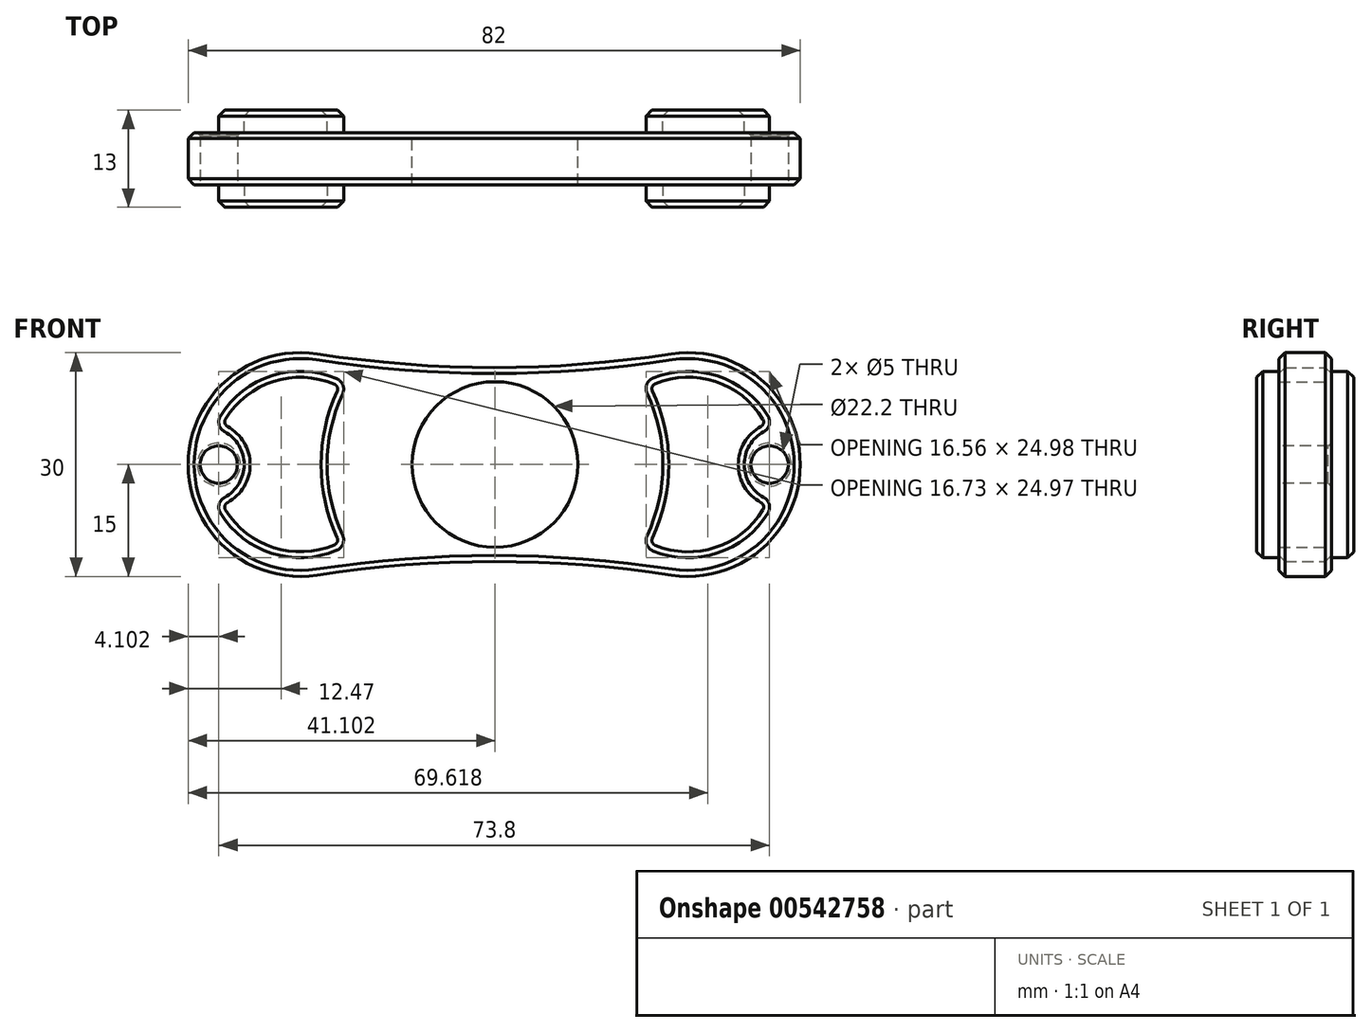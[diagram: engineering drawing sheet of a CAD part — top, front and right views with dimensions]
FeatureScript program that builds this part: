
annotation { "Feature Type Name" : "Feature", "Feature Type Description" : "" }
export const myFeature = defineFeature(function(context is Context, id is Id, definition is map)
    precondition{}
    {
        {
            var Q0;
            Q0=qCreatedBy(makeId("Front.planeOp"),FACE);
            var sketch = newSketch(context, id + "F0", { "sketchPlane" : qUnion([Q0])});
            skCircle(sketch, "E0", {"center": v(-1.84, 0) * mm, "radius": 11.1 * mm});
            skArc(sketch, "E1", {"start": v(-25.64, 14.82) * mm, "mid": v(-42.94, 0) * mm, "end": v(-25.64, -14.82) * mm});
            skArc(sketch, "E2", {"start": v(-25.64, 14.82) * mm, "mid": v(-1.94, 13) * mm, "end": v(21.77, 14.82) * mm});
            skArc(sketch, "E3", {"start": v(21.77, -14.82) * mm, "mid": v(-1.94, -13) * mm, "end": v(-25.64, -14.82) * mm});
            skArc(sketch, "E4.trimOffspring", {"start": v(21.77, -14.82) * mm, "mid": v(39.06, 0) * mm, "end": v(21.77, 14.82) * mm});
            skSolve(sketch);
        }
        {
            var Q0;
            Q0=makeQuery(id+"F0.imprint","IMPRINT",FACE,{"disambiguationData":[TD([[makeQuery(id+"F0.imprint","IMPRINT",EDGE,{"derivedFrom":sQuery(id+"F0.wireOp",EDGE,"E0")}),-1.0]])]});
            extrude(context, id + "F1", {"entities" : qUnion([Q0]), "depth" : 7 * mm, "offsetDistance" : 25 * mm});
        }
        {
            var Q0;
            Q0=makeQuery(id+"F1.opExtrude","CAP_EDGE",EDGE,{"disambiguationData":[OSD([sQuery(id+"F0.wireOp",EDGE,"E1")])],"isStart":false});
            var Q1;
            Q1=makeQuery(id+"F1.opExtrude","CAP_EDGE",EDGE,{"disambiguationData":[OSD([sQuery(id+"F0.wireOp",EDGE,"E3")])],"isStart":false});
            var Q2;
            Q2=makeQuery(id+"F1.opExtrude","CAP_EDGE",EDGE,{"disambiguationData":[OSD([sQuery(id+"F0.wireOp",EDGE,"E3")])],"isStart":true});
            chamfer(context, id + "F2", {"entities" : qUnion([Q0, Q1, Q2]), "width" : .8 * mm, "tangentPropagation" : true});
        }
        {
            var Q0;
            Q0=makeQuery(id+"F1.opExtrude","CAP_FACE",FACE,{"disambiguationData":[OSD([sQuery(id+"F0.wireOp",EDGE,"E0"),sQuery(id+"F0.wireOp",EDGE,"E1"),sQuery(id+"F0.wireOp",EDGE,"E2"),sQuery(id+"F0.wireOp",EDGE,"E3"),sQuery(id+"F0.wireOp",EDGE,"E4.trimOffspring")])],"isStart":false});
            var sketch = newSketch(context, id + "F3", { "sketchPlane" : qUnion([Q0])});
            skCircle(sketch, "E5", {"center": v(-27.94, 0) * mm, "radius": 12.5 * mm});
            skCircle(sketch, "E6", {"center": v(24.06, 0) * mm, "radius": 12.5 * mm});
            skSolve(sketch);
        }
        {
            var Q0;
            Q0 = qSketchRegion(id + "F3", true);
            extrude(context, id + "F4", {"entities" : qUnion([Q0]), "operationType" : NewBodyOperationType.ADD, "depth" : 3 * mm, "offsetDistance" : 25 * mm});
        }
        {
            var Q0;
            Q0=makeQuery(id+"F1.opExtrude","CAP_FACE",FACE,{"disambiguationData":[OSD([sQuery(id+"F0.wireOp",EDGE,"E0"),sQuery(id+"F0.wireOp",EDGE,"E1"),sQuery(id+"F0.wireOp",EDGE,"E2"),sQuery(id+"F0.wireOp",EDGE,"E3"),sQuery(id+"F0.wireOp",EDGE,"E4.trimOffspring")])],"isStart":true});
            var sketch = newSketch(context, id + "F5", { "sketchPlane" : qUnion([Q0])});
            skCircle(sketch, "E7", {"center": v(-24.06, 0) * mm, "radius": 12.5 * mm});
            skCircle(sketch, "E8", {"center": v(27.94, 0) * mm, "radius": 12.5 * mm});
            skSolve(sketch);
        }
        {
            var Q0;
            Q0 = qSketchRegion(id + "F5", true);
            extrude(context, id + "F6", {"entities" : qUnion([Q0]), "operationType" : NewBodyOperationType.ADD, "depth" : 3 * mm, "offsetDistance" : 25 * mm});
        }
        {
            var Q0;
            Q0=makeQuery(id+"F4.opExtrude","CAP_FACE",FACE,{"disambiguationData":[OSD([sQuery(id+"F3.wireOp",EDGE,"E6")])],"isStart":false});
            var sketch = newSketch(context, id + "F7", { "sketchPlane" : qUnion([Q0])});
            skSolve(sketch);
        }
        {
            var Q0;
            Q0=makeQuery(id+"F4.opExtrude","CAP_FACE",FACE,{"disambiguationData":[OSD([sQuery(id+"F3.wireOp",EDGE,"E5")])],"isStart":false});
            var sketch = newSketch(context, id + "F8", { "sketchPlane" : qUnion([Q0])});
            skCircle(sketch, "E9", {"center": v(-1.84, 0) * mm, "radius": 22.5 * mm});
            skSolve(sketch);
        }
        {
            var Q0;
            Q0 = qSketchRegion(id + "F8", true);
            extrude(context, id + "F9", {"entities" : qUnion([Q0]), "operationType" : NewBodyOperationType.REMOVE, "oppositeDirection" : true, "depth" : 3 * mm, "offsetDistance" : 25 * mm});
        }
        {
            var Q0;
            Q0=makeQuery(id+"F6.opExtrude","CAP_FACE",FACE,{"disambiguationData":[OSD([sQuery(id+"F5.wireOp",EDGE,"E7")])],"isStart":false});
            var sketch = newSketch(context, id + "F10", { "sketchPlane" : qUnion([Q0])});
            skCircle(sketch, "E10", {"center": v(1.84, 0) * mm, "radius": 22.5 * mm});
            skSolve(sketch);
        }
        {
            var Q0;
            Q0 = qSketchRegion(id + "F10", true);
            extrude(context, id + "F11", {"entities" : qUnion([Q0]), "operationType" : NewBodyOperationType.REMOVE, "oppositeDirection" : true, "depth" : 3 * mm, "offsetDistance" : 25 * mm});
        }
        {
            var Q0;
            Q0=makeQuery(id+"F6.opExtrude","CAP_FACE",FACE,{"disambiguationData":[OSD([sQuery(id+"F5.wireOp",EDGE,"E7")])],"isStart":false});
            var sketch = newSketch(context, id + "F12", { "sketchPlane" : qUnion([Q0])});
            skCircle(sketch, "E11", {"center": v(-36.56, 0) * mm, "radius": 5 * mm});
            skSolve(sketch);
        }
        {
            var Q0;
            Q0 = qSketchRegion(id + "F12", true);
            extrude(context, id + "F13", {"entities" : qUnion([Q0]), "operationType" : NewBodyOperationType.REMOVE, "oppositeDirection" : true, "depth" : 3 * mm, "offsetDistance" : 25 * mm});
        }
        {
            var Q0;
            Q0=makeQuery(id+"F6.opExtrude","CAP_FACE",FACE,{"disambiguationData":[OSD([sQuery(id+"F5.wireOp",EDGE,"E8")])],"isStart":false});
            var sketch = newSketch(context, id + "F14", { "sketchPlane" : qUnion([Q0])});
            skCircle(sketch, "E12", {"center": v(40.44, 0) * mm, "radius": 5 * mm});
            skSolve(sketch);
        }
        {
            var Q0;
            Q0 = qSketchRegion(id + "F14", true);
            extrude(context, id + "F15", {"entities" : qUnion([Q0]), "operationType" : NewBodyOperationType.REMOVE, "oppositeDirection" : true, "depth" : 3 * mm, "offsetDistance" : 25 * mm});
        }
        {
            var Q0;
            Q0=makeQuery(id+"F4.opExtrude","CAP_FACE",FACE,{"disambiguationData":[OSD([sQuery(id+"F3.wireOp",EDGE,"E5")])],"isStart":false});
            var sketch = newSketch(context, id + "F16", { "sketchPlane" : qUnion([Q0])});
            skCircle(sketch, "E13", {"center": v(-40.44, 0) * mm, "radius": 5 * mm});
            skSolve(sketch);
        }
        {
            var Q0;
            Q0 = qSketchRegion(id + "F16", true);
            extrude(context, id + "F17", {"entities" : qUnion([Q0]), "operationType" : NewBodyOperationType.REMOVE, "oppositeDirection" : true, "depth" : 3 * mm, "offsetDistance" : 25 * mm});
        }
        {
            var Q0;
            Q0=makeQuery(id+"F7.imprint","IMPRINT",FACE,{"disambiguationData":[TD([[makeQuery(id+"F7.imprint","IMPRINT",EDGE,{"derivedFrom":makeQuery(id+"F4.opExtrude","CAP_EDGE",EDGE,{"disambiguationData":[OSD([sQuery(id+"F3.wireOp",EDGE,"E6")])],"isStart":false})}),1.0]])]});
            var sketch = newSketch(context, id + "F18", { "sketchPlane" : qUnion([Q0])});
            skCircle(sketch, "E14", {"center": v(36.56, 0) * mm, "radius": 5 * mm});
            skSolve(sketch);
        }
        {
            var Q0;
            Q0 = qSketchRegion(id + "F18", true);
            extrude(context, id + "F19", {"entities" : qUnion([Q0]), "operationType" : NewBodyOperationType.REMOVE, "oppositeDirection" : true, "depth" : 3 * mm, "offsetDistance" : 25 * mm});
        }
        {
            var Q0;
            Q0=makeQuery(id+"F17.boolean.opBoolean","INTERSECT",EDGE,{"disambiguationData":[OD(0.0)],"derivedFrom":[makeQuery(id+"F4.opExtrude","SWEPT_FACE",FACE,{"disambiguationData":[OSD([sQuery(id+"F3.wireOp",EDGE,"E5")])]}),makeQuery(id+"F17.opExtrude","SWEPT_FACE",FACE,{"disambiguationData":[OSD([sQuery(id+"F16.wireOp",EDGE,"E13")])]})]});
            var Q1;
            Q1=makeQuery(id+"F17.boolean.opBoolean","INTERSECT",EDGE,{"disambiguationData":[OD(1.0)],"derivedFrom":[makeQuery(id+"F4.opExtrude","SWEPT_FACE",FACE,{"disambiguationData":[OSD([sQuery(id+"F3.wireOp",EDGE,"E5")])]}),makeQuery(id+"F17.opExtrude","SWEPT_FACE",FACE,{"disambiguationData":[OSD([sQuery(id+"F16.wireOp",EDGE,"E13")])]})]});
            var Q2;
            Q2=makeQuery(id+"F9.boolean.opBoolean","INTERSECT",EDGE,{"disambiguationData":[OD(1.0)],"derivedFrom":[makeQuery(id+"F4.opExtrude","SWEPT_FACE",FACE,{"disambiguationData":[OSD([sQuery(id+"F3.wireOp",EDGE,"E5")])]}),makeQuery(id+"F9.opExtrude","SWEPT_FACE",FACE,{"disambiguationData":[OSD([sQuery(id+"F8.wireOp",EDGE,"E9")])]})]});
            var Q3;
            Q3=makeQuery(id+"F9.boolean.opBoolean","INTERSECT",EDGE,{"disambiguationData":[OD(0.0)],"derivedFrom":[makeQuery(id+"F4.opExtrude","SWEPT_FACE",FACE,{"disambiguationData":[OSD([sQuery(id+"F3.wireOp",EDGE,"E5")])]}),makeQuery(id+"F9.opExtrude","SWEPT_FACE",FACE,{"disambiguationData":[OSD([sQuery(id+"F8.wireOp",EDGE,"E9")])]})]});
            var Q4;
            Q4=makeQuery(id+"F9.boolean.opBoolean","INTERSECT",EDGE,{"disambiguationData":[OD(1.0)],"derivedFrom":[makeQuery(id+"F4.opExtrude","SWEPT_FACE",FACE,{"disambiguationData":[OSD([sQuery(id+"F3.wireOp",EDGE,"E6")])]}),makeQuery(id+"F9.opExtrude","SWEPT_FACE",FACE,{"disambiguationData":[OSD([sQuery(id+"F8.wireOp",EDGE,"E9")])]})]});
            var Q5;
            Q5=makeQuery(id+"F9.boolean.opBoolean","INTERSECT",EDGE,{"disambiguationData":[OD(0.0)],"derivedFrom":[makeQuery(id+"F4.opExtrude","SWEPT_FACE",FACE,{"disambiguationData":[OSD([sQuery(id+"F3.wireOp",EDGE,"E6")])]}),makeQuery(id+"F9.opExtrude","SWEPT_FACE",FACE,{"disambiguationData":[OSD([sQuery(id+"F8.wireOp",EDGE,"E9")])]})]});
            var Q6;
            Q6=makeQuery(id+"F19.boolean.opBoolean","INTERSECT",EDGE,{"disambiguationData":[OD(1.0)],"derivedFrom":[makeQuery(id+"F4.opExtrude","SWEPT_FACE",FACE,{"disambiguationData":[OSD([sQuery(id+"F3.wireOp",EDGE,"E6")])]}),makeQuery(id+"F19.opExtrude","SWEPT_FACE",FACE,{"disambiguationData":[OSD([sQuery(id+"F18.wireOp",EDGE,"E14")])]})]});
            var Q7;
            Q7=makeQuery(id+"F19.boolean.opBoolean","INTERSECT",EDGE,{"disambiguationData":[OD(0.0)],"derivedFrom":[makeQuery(id+"F4.opExtrude","SWEPT_FACE",FACE,{"disambiguationData":[OSD([sQuery(id+"F3.wireOp",EDGE,"E6")])]}),makeQuery(id+"F19.opExtrude","SWEPT_FACE",FACE,{"disambiguationData":[OSD([sQuery(id+"F18.wireOp",EDGE,"E14")])]})]});
            var Q8;
            Q8=makeQuery(id+"F11.boolean.opBoolean","INTERSECT",EDGE,{"disambiguationData":[OD(0.0)],"derivedFrom":[makeQuery(id+"F6.opExtrude","SWEPT_FACE",FACE,{"disambiguationData":[OSD([sQuery(id+"F5.wireOp",EDGE,"E8")])]}),makeQuery(id+"F11.opExtrude","SWEPT_FACE",FACE,{"disambiguationData":[OSD([sQuery(id+"F10.wireOp",EDGE,"E10")])]})]});
            var Q9;
            Q9=makeQuery(id+"F11.boolean.opBoolean","INTERSECT",EDGE,{"disambiguationData":[OD(1.0)],"derivedFrom":[makeQuery(id+"F6.opExtrude","SWEPT_FACE",FACE,{"disambiguationData":[OSD([sQuery(id+"F5.wireOp",EDGE,"E8")])]}),makeQuery(id+"F11.opExtrude","SWEPT_FACE",FACE,{"disambiguationData":[OSD([sQuery(id+"F10.wireOp",EDGE,"E10")])]})]});
            var Q10;
            Q10=makeQuery(id+"F15.boolean.opBoolean","INTERSECT",EDGE,{"disambiguationData":[OD(0.0)],"derivedFrom":[makeQuery(id+"F6.opExtrude","SWEPT_FACE",FACE,{"disambiguationData":[OSD([sQuery(id+"F5.wireOp",EDGE,"E8")])]}),makeQuery(id+"F15.opExtrude","SWEPT_FACE",FACE,{"disambiguationData":[OSD([sQuery(id+"F14.wireOp",EDGE,"E12")])]})]});
            var Q11;
            Q11=makeQuery(id+"F15.boolean.opBoolean","INTERSECT",EDGE,{"disambiguationData":[OD(1.0)],"derivedFrom":[makeQuery(id+"F6.opExtrude","SWEPT_FACE",FACE,{"disambiguationData":[OSD([sQuery(id+"F5.wireOp",EDGE,"E8")])]}),makeQuery(id+"F15.opExtrude","SWEPT_FACE",FACE,{"disambiguationData":[OSD([sQuery(id+"F14.wireOp",EDGE,"E12")])]})]});
            var Q12;
            Q12=makeQuery(id+"F11.boolean.opBoolean","INTERSECT",EDGE,{"disambiguationData":[OD(0.0)],"derivedFrom":[makeQuery(id+"F6.opExtrude","SWEPT_FACE",FACE,{"disambiguationData":[OSD([sQuery(id+"F5.wireOp",EDGE,"E7")])]}),makeQuery(id+"F11.opExtrude","SWEPT_FACE",FACE,{"disambiguationData":[OSD([sQuery(id+"F10.wireOp",EDGE,"E10")])]})]});
            var Q13;
            Q13=makeQuery(id+"F11.boolean.opBoolean","INTERSECT",EDGE,{"disambiguationData":[OD(1.0)],"derivedFrom":[makeQuery(id+"F6.opExtrude","SWEPT_FACE",FACE,{"disambiguationData":[OSD([sQuery(id+"F5.wireOp",EDGE,"E7")])]}),makeQuery(id+"F11.opExtrude","SWEPT_FACE",FACE,{"disambiguationData":[OSD([sQuery(id+"F10.wireOp",EDGE,"E10")])]})]});
            var Q14;
            Q14=makeQuery(id+"F13.boolean.opBoolean","INTERSECT",EDGE,{"disambiguationData":[OD(0.0)],"derivedFrom":[makeQuery(id+"F6.opExtrude","SWEPT_FACE",FACE,{"disambiguationData":[OSD([sQuery(id+"F5.wireOp",EDGE,"E7")])]}),makeQuery(id+"F13.opExtrude","SWEPT_FACE",FACE,{"disambiguationData":[OSD([sQuery(id+"F12.wireOp",EDGE,"E11")])]})]});
            var Q15;
            Q15=makeQuery(id+"F13.boolean.opBoolean","INTERSECT",EDGE,{"disambiguationData":[OD(1.0)],"derivedFrom":[makeQuery(id+"F6.opExtrude","SWEPT_FACE",FACE,{"disambiguationData":[OSD([sQuery(id+"F5.wireOp",EDGE,"E7")])]}),makeQuery(id+"F13.opExtrude","SWEPT_FACE",FACE,{"disambiguationData":[OSD([sQuery(id+"F12.wireOp",EDGE,"E11")])]})]});
            fillet(context, id + "F20", {"entities" : qUnion([Q0, Q1, Q2, Q3, Q4, Q5, Q6, Q7, Q8, Q9, Q10, Q11, Q12, Q13, Q14, Q15]), "radius" : 1.5 * mm, "tangentPropagation" : true, "allowEdgeOverflow" : false});
        }
        {
            var Q0;
            Q0=makeQuery(id+"F19.boolean.opBoolean","MERGE",FACE,{"derivedFrom":[makeQuery(id+"F17.boolean.opBoolean","MERGE",FACE,{"derivedFrom":[makeQuery(id+"F9.boolean.opBoolean","MERGE",FACE,{"derivedFrom":[makeQuery(id+"F1.opExtrude","CAP_FACE",FACE,{"disambiguationData":[OSD([sQuery(id+"F0.wireOp",EDGE,"E0"),sQuery(id+"F0.wireOp",EDGE,"E1"),sQuery(id+"F0.wireOp",EDGE,"E2"),sQuery(id+"F0.wireOp",EDGE,"E3"),sQuery(id+"F0.wireOp",EDGE,"E4.trimOffspring")])],"isStart":false}),makeQuery(id+"F9.opExtrude","CAP_FACE",FACE,{"disambiguationData":[OSD([sQuery(id+"F8.wireOp",EDGE,"E9")])],"isStart":false})]}),makeQuery(id+"F17.opExtrude","CAP_FACE",FACE,{"disambiguationData":[OSD([sQuery(id+"F16.wireOp",EDGE,"E13")])],"isStart":false})]}),makeQuery(id+"F19.opExtrude","CAP_FACE",FACE,{"disambiguationData":[OSD([sQuery(id+"F18.wireOp",EDGE,"E14")])],"isStart":false})]});
            var sketch = newSketch(context, id + "F21", { "sketchPlane" : qUnion([Q0])});
            skCircle(sketch, "E15", {"center": v(-38.84, 0) * mm, "radius": 2.5 * mm});
            skSolve(sketch);
        }
        {
            var Q0;
            Q0 = qSketchRegion(id + "F21", true);
            extrude(context, id + "F22", {"entities" : qUnion([Q0]), "operationType" : NewBodyOperationType.REMOVE, "oppositeDirection" : true, "depth" : 25 * mm, "offsetDistance" : 25 * mm});
        }
        {
            var Q0;
            Q0=makeQuery(id+"F19.boolean.opBoolean","MERGE",FACE,{"derivedFrom":[makeQuery(id+"F17.boolean.opBoolean","MERGE",FACE,{"derivedFrom":[makeQuery(id+"F9.boolean.opBoolean","MERGE",FACE,{"derivedFrom":[makeQuery(id+"F1.opExtrude","CAP_FACE",FACE,{"disambiguationData":[OSD([sQuery(id+"F0.wireOp",EDGE,"E0"),sQuery(id+"F0.wireOp",EDGE,"E1"),sQuery(id+"F0.wireOp",EDGE,"E2"),sQuery(id+"F0.wireOp",EDGE,"E3"),sQuery(id+"F0.wireOp",EDGE,"E4.trimOffspring")])],"isStart":false}),makeQuery(id+"F9.opExtrude","CAP_FACE",FACE,{"disambiguationData":[OSD([sQuery(id+"F8.wireOp",EDGE,"E9")])],"isStart":false})]}),makeQuery(id+"F17.opExtrude","CAP_FACE",FACE,{"disambiguationData":[OSD([sQuery(id+"F16.wireOp",EDGE,"E13")])],"isStart":false})]}),makeQuery(id+"F19.opExtrude","CAP_FACE",FACE,{"disambiguationData":[OSD([sQuery(id+"F18.wireOp",EDGE,"E14")])],"isStart":false})]});
            var sketch = newSketch(context, id + "F23", { "sketchPlane" : qUnion([Q0])});
            skCircle(sketch, "E16", {"center": v(34.96, 0) * mm, "radius": 2.5 * mm});
            skSolve(sketch);
        }
        {
            var Q0;
            Q0 = qSketchRegion(id + "F23", true);
            extrude(context, id + "F24", {"entities" : qUnion([Q0]), "operationType" : NewBodyOperationType.REMOVE, "oppositeDirection" : true, "depth" : 25 * mm, "offsetDistance" : 25 * mm});
        }
        {
            var Q0;
            Q0=makeQuery(id+"F22.boolean.opBoolean","COPY",EDGE,{"derivedFrom":makeQuery(id+"F22.opExtrude","CAP_EDGE",EDGE,{"disambiguationData":[OSD([sQuery(id+"F21.wireOp",EDGE,"E15")])],"isStart":true})});
            var Q1;
            Q1=makeQuery(id+"F24.boolean.opBoolean","COPY",EDGE,{"derivedFrom":makeQuery(id+"F24.opExtrude","CAP_EDGE",EDGE,{"disambiguationData":[OSD([sQuery(id+"F23.wireOp",EDGE,"E16")])],"isStart":true})});
            var Q2;
            Q2=makeQuery(id+"F24.boolean.opBoolean","INTERSECT",EDGE,{"derivedFrom":[makeQuery(id+"F15.boolean.opBoolean","MERGE",FACE,{"derivedFrom":[makeQuery(id+"F13.boolean.opBoolean","MERGE",FACE,{"derivedFrom":[makeQuery(id+"F11.boolean.opBoolean","MERGE",FACE,{"derivedFrom":[makeQuery(id+"F1.opExtrude","CAP_FACE",FACE,{"disambiguationData":[OSD([sQuery(id+"F0.wireOp",EDGE,"E0"),sQuery(id+"F0.wireOp",EDGE,"E1"),sQuery(id+"F0.wireOp",EDGE,"E2"),sQuery(id+"F0.wireOp",EDGE,"E3"),sQuery(id+"F0.wireOp",EDGE,"E4.trimOffspring")])],"isStart":true}),makeQuery(id+"F11.opExtrude","CAP_FACE",FACE,{"disambiguationData":[OSD([sQuery(id+"F10.wireOp",EDGE,"E10")])],"isStart":false})]}),makeQuery(id+"F13.opExtrude","CAP_FACE",FACE,{"disambiguationData":[OSD([sQuery(id+"F12.wireOp",EDGE,"E11")])],"isStart":false})]}),makeQuery(id+"F15.opExtrude","CAP_FACE",FACE,{"disambiguationData":[OSD([sQuery(id+"F14.wireOp",EDGE,"E12")])],"isStart":false})]}),makeQuery(id+"F24.opExtrude","SWEPT_FACE",FACE,{"disambiguationData":[OSD([sQuery(id+"F23.wireOp",EDGE,"E16")])]})]});
            var Q3;
            Q3=makeQuery(id+"F22.boolean.opBoolean","INTERSECT",EDGE,{"derivedFrom":[makeQuery(id+"F15.boolean.opBoolean","MERGE",FACE,{"derivedFrom":[makeQuery(id+"F13.boolean.opBoolean","MERGE",FACE,{"derivedFrom":[makeQuery(id+"F11.boolean.opBoolean","MERGE",FACE,{"derivedFrom":[makeQuery(id+"F1.opExtrude","CAP_FACE",FACE,{"disambiguationData":[OSD([sQuery(id+"F0.wireOp",EDGE,"E0"),sQuery(id+"F0.wireOp",EDGE,"E1"),sQuery(id+"F0.wireOp",EDGE,"E2"),sQuery(id+"F0.wireOp",EDGE,"E3"),sQuery(id+"F0.wireOp",EDGE,"E4.trimOffspring")])],"isStart":true}),makeQuery(id+"F11.opExtrude","CAP_FACE",FACE,{"disambiguationData":[OSD([sQuery(id+"F10.wireOp",EDGE,"E10")])],"isStart":false})]}),makeQuery(id+"F13.opExtrude","CAP_FACE",FACE,{"disambiguationData":[OSD([sQuery(id+"F12.wireOp",EDGE,"E11")])],"isStart":false})]}),makeQuery(id+"F15.opExtrude","CAP_FACE",FACE,{"disambiguationData":[OSD([sQuery(id+"F14.wireOp",EDGE,"E12")])],"isStart":false})]}),makeQuery(id+"F22.opExtrude","SWEPT_FACE",FACE,{"disambiguationData":[OSD([sQuery(id+"F21.wireOp",EDGE,"E15")])]})]});
            chamfer(context, id + "F25", {"entities" : qUnion([Q0, Q1, Q2, Q3]), "width" : 0.4 * mm, "tangentPropagation" : true});
        }
        {
            var Q0;
            Q0=makeQuery(id+"F4.opExtrude","CAP_FACE",FACE,{"disambiguationData":[OSD([sQuery(id+"F3.wireOp",EDGE,"E6")])],"isStart":false});
            var Q1;
            Q1=makeQuery(id+"F4.opExtrude","CAP_FACE",FACE,{"disambiguationData":[OSD([sQuery(id+"F3.wireOp",EDGE,"E5")])],"isStart":false});
            var Q2;
            Q2=makeQuery(id+"F6.opExtrude","CAP_FACE",FACE,{"disambiguationData":[OSD([sQuery(id+"F5.wireOp",EDGE,"E8")])],"isStart":false});
            var Q3;
            Q3=makeQuery(id+"F6.opExtrude","CAP_FACE",FACE,{"disambiguationData":[OSD([sQuery(id+"F5.wireOp",EDGE,"E7")])],"isStart":false});
            chamfer(context, id + "F26", {"entities" : qUnion([Q0, Q1, Q2, Q3]), "width" : .8 * mm, "tangentPropagation" : true});
        }
    });
